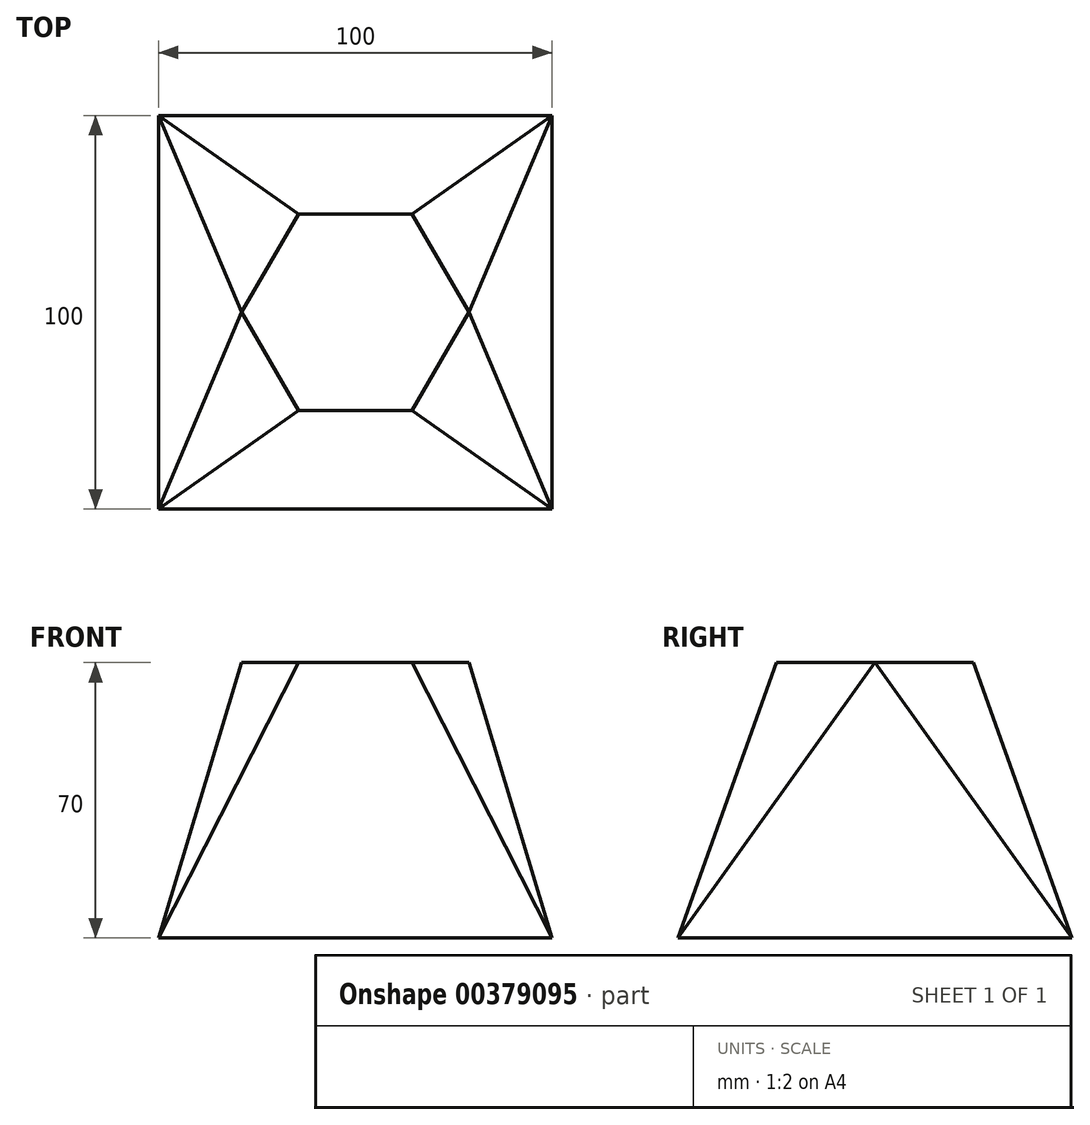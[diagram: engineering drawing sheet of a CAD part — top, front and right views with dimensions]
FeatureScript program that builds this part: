
annotation { "Feature Type Name" : "Feature", "Feature Type Description" : "" }
export const myFeature = defineFeature(function(context is Context, id is Id, definition is map)
    precondition{}
    {
        {
            var Q0;
            Q0=qCreatedBy(makeId("Top.planeOp"),FACE);
            var sketch = newSketch(context, id + "F0", { "sketchPlane" : qUnion([Q0])});
            skLineSegment(sketch, "E0.bottom", {"start": v(50, -50) * mm, "end": v(-50, -50) * mm});
            skLineSegment(sketch, "E0.top", {"start": v(50, 50) * mm, "end": v(-50, 50) * mm});
            skLineSegment(sketch, "E0.left", {"start": v(50, -50) * mm, "end": v(50, 50) * mm});
            skLineSegment(sketch, "E0.right", {"start": v(-50, -50) * mm, "end": v(-50, 50) * mm});
            skPoint(sketch, "E0.middle", {"position": v(0, 0) * mm});
            skSolve(sketch);
        }
        {
            var Q0;
            Q0=qCreatedBy(makeId("Top.planeOp"),FACE);
            cPlane(context, id + "F1", {"entities" : qUnion([Q0]), "cplaneType" : CPlaneType.OFFSET, "offset" : 70 * mm, "width" : 150 * mm, "height" : 150 * mm});
        }
        {
            var Q0;
            Q0=qCreatedBy(id+"F1.planeOp",FACE);
            var sketch = newSketch(context, id + "F2", { "sketchPlane" : qUnion([Q0])});
            skCircle(sketch, "E1.cCircle", {"center": v(0, 0) * mm, "radius": 28.87 * mm, "construction": true});
            skLineSegment(sketch, "E1.0", {"start": v(28.87, 0) * mm, "end": v(14.43, -25) * mm});
            skLineSegment(sketch, "E1.1", {"start": v(14.43, -25) * mm, "end": v(-14.43, -25) * mm});
            skLineSegment(sketch, "E1.2", {"start": v(-14.43, -25) * mm, "end": v(-28.87, 0) * mm});
            skLineSegment(sketch, "E1.3", {"start": v(-28.87, 0) * mm, "end": v(-14.43, 25) * mm});
            skLineSegment(sketch, "E1.4", {"start": v(-14.43, 25) * mm, "end": v(14.43, 25) * mm});
            skLineSegment(sketch, "E1.5", {"start": v(14.43, 25) * mm, "end": v(28.87, 0) * mm});
            skLineSegment(sketch, "E2", {"start": v(28.87, 25) * mm, "end": v(28.87, 0) * mm});
            skLineSegment(sketch, "E3", {"start": v(28.87, -25) * mm, "end": v(28.87, 0) * mm});
            skLineSegment(sketch, "E4", {"start": v(-14.43, 25) * mm, "end": v(-28.87, 25) * mm});
            skLineSegment(sketch, "E5", {"start": v(-28.87, 25) * mm, "end": v(-28.87, 0) * mm});
            skLineSegment(sketch, "E6", {"start": v(-14.43, -25) * mm, "end": v(-28.87, -25) * mm});
            skLineSegment(sketch, "E7", {"start": v(-28.87, -25) * mm, "end": v(-28.87, 0) * mm});
            skLineSegment(sketch, "E8", {"start": v(28.87, 25) * mm, "end": v(14.43, 25) * mm});
            skLineSegment(sketch, "E9", {"start": v(28.87, -25) * mm, "end": v(14.43, -25) * mm});
            skSolve(sketch);
        }
        {
            var Q0;
            Q0=qCreatedBy(id+"F1.planeOp",FACE);
            var sketch = newSketch(context, id + "F3", { "sketchPlane" : qUnion([Q0])});
            skLineSegment(sketch, "E10.bottom", {"start": v(28.87, -25) * mm, "end": v(-28.87, -25) * mm});
            skLineSegment(sketch, "E10.top", {"start": v(28.87, 25) * mm, "end": v(-28.87, 25) * mm});
            skLineSegment(sketch, "E10.left", {"start": v(28.87, -25) * mm, "end": v(28.87, 25) * mm});
            skLineSegment(sketch, "E10.right", {"start": v(-28.87, -25) * mm, "end": v(-28.87, 25) * mm});
            skPoint(sketch, "E10.middle", {"position": v(0, 0) * mm});
            skSolve(sketch);
        }
        {
            var Q0;
            Q0 = qSketchRegion(id + "F3", true);
            var Q1;
            Q1=makeQuery(id+"F0.imprint","IMPRINT",FACE,{"disambiguationData":[TD([[makeQuery(id+"F0.imprint","IMPRINT",EDGE,{"derivedFrom":sQuery(id+"F0.wireOp",EDGE,"E0.bottom")}),-1.0]])]});
            loft(context, id + "F4", {"sheetProfilesArray" : [{ "sheetProfileEntities" : qUnion([Q0]) }, { "sheetProfileEntities" : qUnion([Q1]) }]});
        }
        {
            var Q1;
            Q1=makeQuery(id+"F2.imprint","IMPRINT",FACE,{"disambiguationData":[TD([[makeQuery(id+"F2.imprint","IMPRINT",EDGE,{"derivedFrom":sQuery(id+"F2.wireOp",EDGE,"E1.0")}),1.0]])]});
            var Q2;
            Q2=makeQuery(id+"F4.opLoft","MID_CAP_VERTEX",VERTEX,{"disambiguationData":[OSD([sQuery(id+"F0.wireOp",EDGE,"E0.bottom"),sQuery(id+"F0.wireOp",EDGE,"E0.left")])],"capPos":1.0});
            loft(context, id + "F5", {"sheetProfilesArray" : [{ "sheetProfileEntities" : qUnion([Q1]) }, { "sheetProfileEntities" : qUnion([Q2]) }]});
        }
        {
            var Q0;
            Q0=makeQuery(id+"F5.opLoft","SWEPT_BODY",BODY,{"disambiguationData":[OSD([sQuery(id+"F0.wireOp",EDGE,"E0.bottom"),sQuery(id+"F0.wireOp",EDGE,"E0.left"),makeQuery(id+"F2.imprint","IMPRINT",FACE,{"disambiguationData":[TD([[makeQuery(id+"F2.imprint","IMPRINT",EDGE,{"derivedFrom":sQuery(id+"F2.wireOp",EDGE,"E1.0")}),1.0]])]})])]});
            var Q1;
            Q1=qCreatedBy(makeId("Front.planeOp"),FACE);
            mirror(context, id + "F6", {"entities" : qUnion([Q0]), "mirrorPlane" : qUnion([Q1])});
        }
        {
            var Q0;
            Q0=makeQuery(id+"F5.opLoft","SWEPT_BODY",BODY,{"disambiguationData":[OSD([sQuery(id+"F0.wireOp",EDGE,"E0.bottom"),sQuery(id+"F0.wireOp",EDGE,"E0.left"),makeQuery(id+"F2.imprint","IMPRINT",FACE,{"disambiguationData":[TD([[makeQuery(id+"F2.imprint","IMPRINT",EDGE,{"derivedFrom":sQuery(id+"F2.wireOp",EDGE,"E1.0")}),1.0]])]})])]});
            var Q1;
            Q1=makeQuery(id+"F6.opPattern","COPY",BODY,{"derivedFrom":makeQuery(id+"F5.opLoft","SWEPT_BODY",BODY,{"disambiguationData":[OSD([sQuery(id+"F0.wireOp",EDGE,"E0.bottom"),sQuery(id+"F0.wireOp",EDGE,"E0.left"),makeQuery(id+"F2.imprint","IMPRINT",FACE,{"disambiguationData":[TD([[makeQuery(id+"F2.imprint","IMPRINT",EDGE,{"derivedFrom":sQuery(id+"F2.wireOp",EDGE,"E1.0")}),1.0]])]})])]}),"instanceName":"1"});
            var Q2;
            Q2=qCreatedBy(makeId("Right.planeOp"),FACE);
            mirror(context, id + "F7", {"entities" : qUnion([Q0, Q1]), "mirrorPlane" : qUnion([Q2])});
        }
        {
            var Q0;
            Q0=makeQuery(id+"F5.opLoft","SWEPT_BODY",BODY,{"disambiguationData":[OSD([sQuery(id+"F0.wireOp",EDGE,"E0.bottom"),sQuery(id+"F0.wireOp",EDGE,"E0.left"),makeQuery(id+"F2.imprint","IMPRINT",FACE,{"disambiguationData":[TD([[makeQuery(id+"F2.imprint","IMPRINT",EDGE,{"derivedFrom":sQuery(id+"F2.wireOp",EDGE,"E1.0")}),1.0]])]})])]});
            var Q1;
            Q1=makeQuery(id+"F6.opPattern","COPY",BODY,{"derivedFrom":makeQuery(id+"F5.opLoft","SWEPT_BODY",BODY,{"disambiguationData":[OSD([sQuery(id+"F0.wireOp",EDGE,"E0.bottom"),sQuery(id+"F0.wireOp",EDGE,"E0.left"),makeQuery(id+"F2.imprint","IMPRINT",FACE,{"disambiguationData":[TD([[makeQuery(id+"F2.imprint","IMPRINT",EDGE,{"derivedFrom":sQuery(id+"F2.wireOp",EDGE,"E1.0")}),1.0]])]})])]}),"instanceName":"1"});
            var Q2;
            Q2=makeQuery(id+"F7.opPattern","COPY",BODY,{"derivedFrom":makeQuery(id+"F5.opLoft","SWEPT_BODY",BODY,{"disambiguationData":[OSD([sQuery(id+"F0.wireOp",EDGE,"E0.bottom"),sQuery(id+"F0.wireOp",EDGE,"E0.left"),makeQuery(id+"F2.imprint","IMPRINT",FACE,{"disambiguationData":[TD([[makeQuery(id+"F2.imprint","IMPRINT",EDGE,{"derivedFrom":sQuery(id+"F2.wireOp",EDGE,"E1.0")}),1.0]])]})])]}),"instanceName":"1"});
            var Q3;
            Q3=makeQuery(id+"F7.opPattern","COPY",BODY,{"derivedFrom":makeQuery(id+"F6.opPattern","COPY",BODY,{"derivedFrom":makeQuery(id+"F5.opLoft","SWEPT_BODY",BODY,{"disambiguationData":[OSD([sQuery(id+"F0.wireOp",EDGE,"E0.bottom"),sQuery(id+"F0.wireOp",EDGE,"E0.left"),makeQuery(id+"F2.imprint","IMPRINT",FACE,{"disambiguationData":[TD([[makeQuery(id+"F2.imprint","IMPRINT",EDGE,{"derivedFrom":sQuery(id+"F2.wireOp",EDGE,"E1.0")}),1.0]])]})])]}),"instanceName":"1"}),"instanceName":"1"});
            var Q4;
            Q4=makeQuery(id+"F4.opLoft","SWEPT_BODY",BODY,{"disambiguationData":[OSD([makeQuery(id+"F0.imprint","IMPRINT",FACE,{"disambiguationData":[TD([[makeQuery(id+"F0.imprint","IMPRINT",EDGE,{"derivedFrom":sQuery(id+"F0.wireOp",EDGE,"E0.bottom")}),-1.0]])]}),makeQuery(id+"F3.imprint","IMPRINT",FACE,{"disambiguationData":[TD([[makeQuery(id+"F3.imprint","IMPRINT",EDGE,{"derivedFrom":sQuery(id+"F3.wireOp",EDGE,"E10.bottom")}),-1.0]])]})])]});
            booleanBodies(context, id + "F8", {"operationType" : BooleanOperationType.SUBTRACTION, "tools" : qUnion([Q0, Q1, Q2, Q3]), "targets" : qUnion([Q4])});
        }
    });
